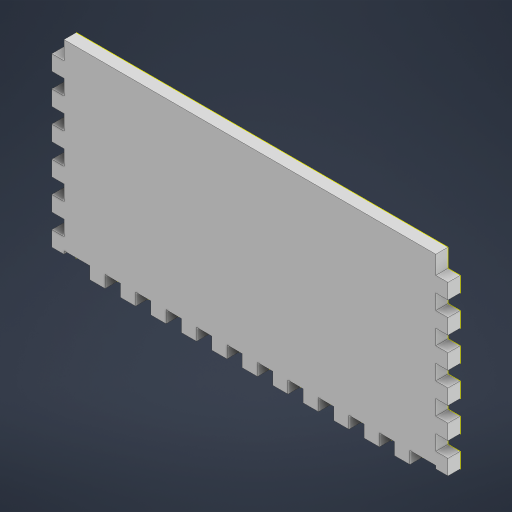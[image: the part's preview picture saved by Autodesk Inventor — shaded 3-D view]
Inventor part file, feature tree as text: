
AUTODESK INVENTOR PART (.ipt)
format: ipt  version: 2023 (Build 270158030, 158C)  size: 320,000 bytes
history: native  units: mm
features: sketch x2, extrude x1, projected_geometry x1
ambient origin geometry x8: Origin, YZ Plane, XZ Plane, XY Plane, X Axis, Y Axis, Z Axis, Center Point
bodies: Solid1 (feature_tree)
feature tree (4):
  extrude  "Extrusion1"  [1 undecoded]
  sketch  "Sketch2"
  sketch  "Sketch1"  dims[d0=4.0mm d1=0.0mm]
  projected_geometry  "Projected Loop1"
note: 1 required parameter value undecoded (feature->parameter linkage not recoverable at this tier; creation-order binding heuristic only, values carry confidence <= 0.55)
